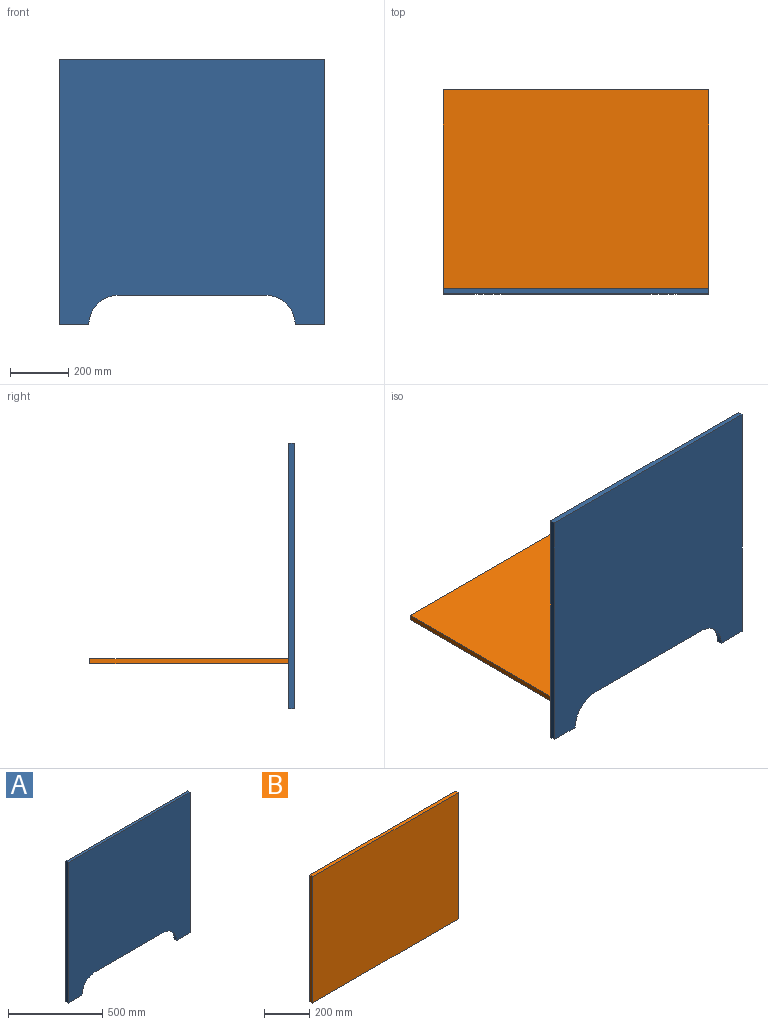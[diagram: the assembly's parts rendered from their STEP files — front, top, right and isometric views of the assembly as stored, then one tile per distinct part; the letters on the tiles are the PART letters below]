
ASSEMBLY  parts=2 mates=1
PART A: 10 faces, bbox 914.4x18.3x914.4 mm
  f0: plane 101.6x18.26mm, normal (0,0,-1), area 1854.8mm2, adj f1,f2,f6,f8
  f1: plane 914.4x914.4mm, normal (0,-1,0), area 768299.9mm2, adj f0,f3,f4,f5,f6,f7,f8,f9
  f2: plane 914.4x914.4mm, normal (0,1,0), area 768299.9mm2, adj f0,f3,f4,f5,f6,f7,f8,f9
  f3: plane 101.6x18.26mm, normal (0,0,-1), area 1854.8mm2, adj f1,f2,f4,f9
  f4: plane 914.4x18.26mm, normal (1,0,0), area 16693.5mm2, adj f1,f2,f3,f5
  f5: plane 914.4x18.26mm, normal (0,0,1), area 16693.5mm2, adj f1,f2,f4,f6
  f6: plane 914.4x18.26mm, normal (-1,0,0), area 16693.5mm2, adj f0,f1,f2,f5
  f7: plane 508x18.26mm, normal (0,0,-1), area 9274.2mm2, adj f1,f2,f8,f9
  f8: cylinder r=101.6mm len=101.6mm, axis (0,-1,0), area 2913.6mm2, adj f0,f1,f2,f7
  f9: cylinder r=101.6mm len=101.6mm, axis (0,-1,0), area 2913.6mm2, adj f1,f2,f3,f7
PART B: 6 faces, bbox 914.4x18.3x685.8 mm
  f0: plane 685.8x18.26mm, normal (1,0,0), area 12520.1mm2, adj f1,f3,f4,f5
  f1: plane 914.4x18.26mm, normal (0,0,1), area 16693.5mm2, adj f0,f2,f4,f5
  f2: plane 685.8x18.26mm, normal (-1,0,0), area 12520.1mm2, adj f1,f3,f4,f5
  f3: plane 914.4x18.26mm, normal (0,0,-1), area 16693.5mm2, adj f0,f2,f4,f5
  f4: plane 914.4x685.8mm, normal (0,-1,0), area 627095.5mm2, adj f0,f1,f2,f3
  f5: plane 914.4x685.8mm, normal (0,1,0), area 627095.5mm2, adj f0,f1,f2,f3
PLACE A t=(-375.45,-371.27,65.81)mm
PLACE B rot(axis=(1,0,0),90deg) t=(-375.45,-28.37,-219.22)mm
MATE planar B.f1 <-> A.f2  axis (0,-1,0) through (-375.45,-371.27,-228.35)mm
